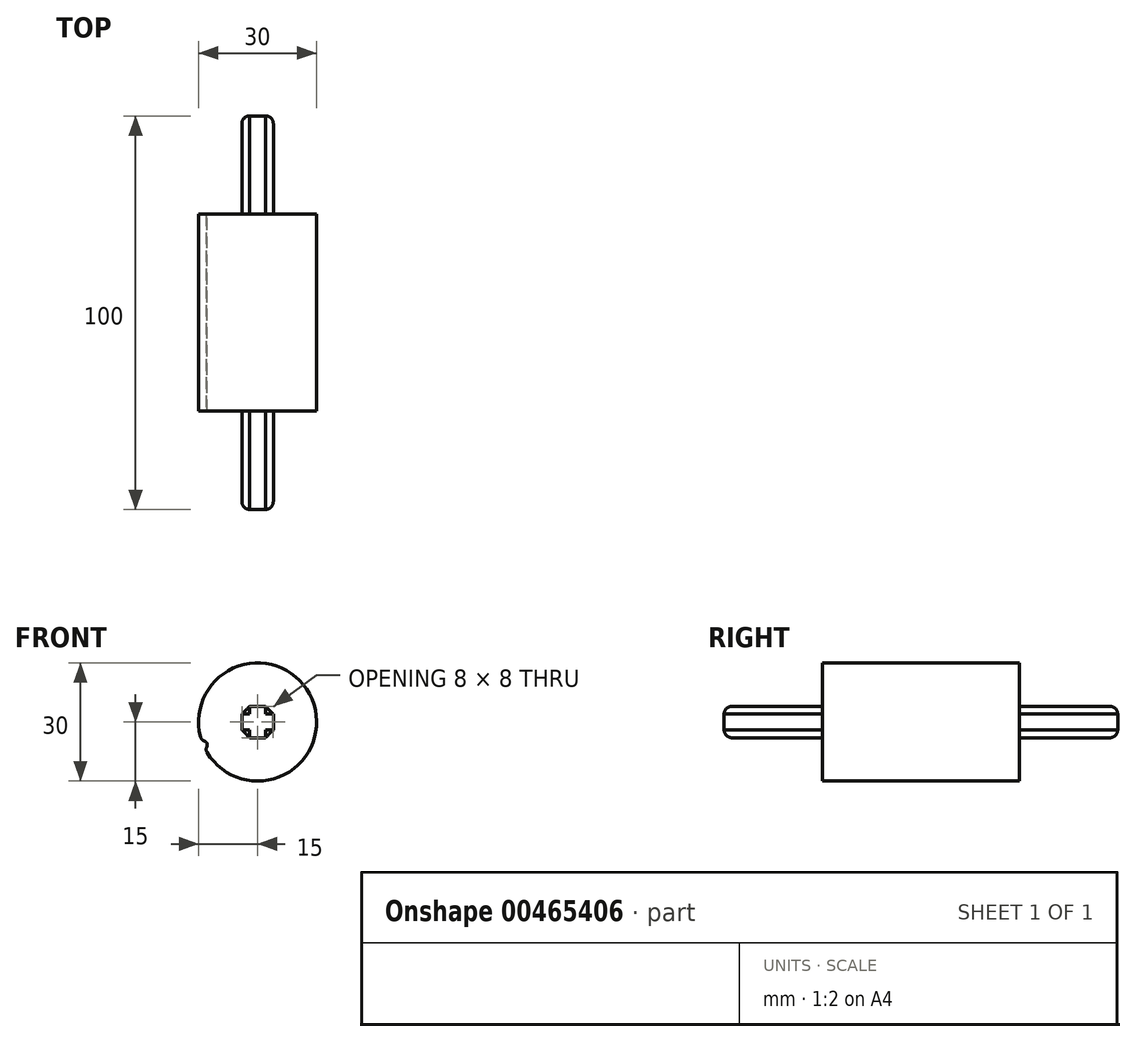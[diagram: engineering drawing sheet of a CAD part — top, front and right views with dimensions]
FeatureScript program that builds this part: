
annotation { "Feature Type Name" : "Feature", "Feature Type Description" : "" }
export const myFeature = defineFeature(function(context is Context, id is Id, definition is map)
    precondition{}
    {
        {
            var Q0;
            Q0=qCreatedBy(makeId("Front.planeOp"),FACE);
            var sketch = newSketch(context, id + "F0", { "sketchPlane" : qUnion([Q0])});
            skCircle(sketch, "E0", {"center": v(0, 0) * mm, "radius": 15 * mm});
            skSolve(sketch);
        }
        {
            var Q0;
            Q0 = qSketchRegion(id + "F0", true);
            extrude(context, id + "F1", {"entities" : qUnion([Q0]), "depth" : 25 * mm});
        }
        {
            var Q0;
            Q0=makeQuery(id+"F1.opExtrude","CAP_FACE",FACE,{"disambiguationData":[OSD([sQuery(id+"F0.wireOp",EDGE,"E0")])],"isStart":false});
            var sketch = newSketch(context, id + "F2", { "sketchPlane" : qUnion([Q0])});
            skLineSegment(sketch, "E1.bottom", {"start": v(4, -4) * mm, "end": v(-4, -4) * mm});
            skLineSegment(sketch, "E1.top", {"start": v(4, 4) * mm, "end": v(-4, 4) * mm});
            skLineSegment(sketch, "E1.left", {"start": v(4, -4) * mm, "end": v(4, 4) * mm});
            skLineSegment(sketch, "E1.right", {"start": v(-4, -4) * mm, "end": v(-4, 4) * mm});
            skCircle(sketch, "E2", {"center": v(13.4, -6.73) * mm, "radius": 1 * mm});
            skSolve(sketch);
        }
        {
            var Q0;
            Q0=makeQuery(id+"F2.imprint","IMPRINT",FACE,{"disambiguationData":[TD([[makeQuery(id+"F2.imprint","IMPRINT",EDGE,{"derivedFrom":sQuery(id+"F2.wireOp",EDGE,"E1.bottom")}),-1.0]])]});
            extrude(context, id + "F3", {"entities" : qUnion([Q0]), "operationType" : NewBodyOperationType.ADD, "depth" : 25 * mm});
        }
        {
            var Q0;
            Q0=makeQuery(id+"F1.opExtrude","CAP_FACE",FACE,{"disambiguationData":[OSD([sQuery(id+"F0.wireOp",EDGE,"E0")])],"isStart":true});
            var sketch = newSketch(context, id + "F4", { "sketchPlane" : qUnion([Q0])});
            skCircle(sketch, "E3", {"center": v(13.82, -5.83) * mm, "radius": 1.04 * mm});
            skSolve(sketch);
        }
        {
            var Q0;
            {var subQ0=sQuery(id+"F4.wireOp",EDGE,"E3");var subQ1=makeQuery(id+"F1.opExtrude","CAP_EDGE",EDGE,{"disambiguationData":[OSD([sQuery(id+"F0.wireOp",EDGE,"E0")])],"isStart":true});var subQ2=makeQuery(id+"F4.imprint","INTERSECT",VERTEX,{"disambiguationData":[OD(0.0)],"derivedFrom":[subQ1,subQ0]});Q0=makeQuery(id+"F4.imprint","IMPRINT",FACE,{"disambiguationData":[TD([[makeQuery(id+"F4.imprint","IMPRINT",EDGE,{"disambiguationData":[TD([[subQ2,1.0]])],"derivedFrom":subQ0}),1.0]])]});}
            var Q1;
            {var subQ0=sQuery(id+"F4.wireOp",EDGE,"E3");var subQ1=makeQuery(id+"F1.opExtrude","CAP_EDGE",EDGE,{"disambiguationData":[OSD([sQuery(id+"F0.wireOp",EDGE,"E0")])],"isStart":true});var subQ2=makeQuery(id+"F4.imprint","INTERSECT",VERTEX,{"disambiguationData":[OD(0.0)],"derivedFrom":[subQ1,subQ0]});Q1=makeQuery(id+"F4.imprint","IMPRINT",FACE,{"disambiguationData":[TD([[makeQuery(id+"F4.imprint","IMPRINT",EDGE,{"disambiguationData":[TD([[subQ2,-1.0]])],"derivedFrom":subQ0}),1.0]])]});}
            var Q2;
            Q2=sQuery(id+"F4.wireOp",EDGE,"E3");
            extrude(context, id + "F5", {"entities" : qUnion([Q0, Q1]), "operationType" : NewBodyOperationType.REMOVE, "surfaceEntities" : qUnion([Q2]), "oppositeDirection" : true, "depth" : 25 * mm});
        }
        {
            var Q0;
            Q0=qCreatedBy(makeId("Right.planeOp"),FACE);
            var sketch = newSketch(context, id + "F6", { "sketchPlane" : qUnion([Q0])});
            skLineSegment(sketch, "E4", {"start": v(0, 0) * mm, "end": v(-24.96, 0) * mm});
            skSolve(sketch);
        }
        {
            var Q0;
            Q0=makeQuery(id+"F3.opExtrude","CAP_EDGE",EDGE,{"disambiguationData":[OSD([sQuery(id+"F2.wireOp",EDGE,"E1.left")])],"isStart":false});
            var Q1;
            Q1=makeQuery(id+"F3.opExtrude","CAP_EDGE",EDGE,{"disambiguationData":[OSD([sQuery(id+"F2.wireOp",EDGE,"E1.bottom")])],"isStart":false});
            var Q2;
            Q2=makeQuery(id+"F3.opExtrude","CAP_EDGE",EDGE,{"disambiguationData":[OSD([sQuery(id+"F2.wireOp",EDGE,"E1.right")])],"isStart":false});
            var Q3;
            Q3=makeQuery(id+"F3.opExtrude","CAP_EDGE",EDGE,{"disambiguationData":[OSD([sQuery(id+"F2.wireOp",EDGE,"E1.top")])],"isStart":false});
            fillet(context, id + "F7", {"entities" : qUnion([Q0, Q1, Q2, Q3]), "radius" : 2 * mm, "tangentPropagation" : true, "allowEdgeOverflow" : false});
        }
        {
            var Q0;
            Q0=makeQuery(id+"F3.opExtrude","SWEPT_EDGE",EDGE,{"disambiguationData":[OSD([sQuery(id+"F2.wireOp",EDGE,"E1.bottom"),sQuery(id+"F2.wireOp",EDGE,"E1.left")])]});
            var Q1;
            Q1=makeQuery(id+"F3.opExtrude","SWEPT_EDGE",EDGE,{"disambiguationData":[OSD([sQuery(id+"F2.wireOp",EDGE,"E1.top"),sQuery(id+"F2.wireOp",EDGE,"E1.left")])]});
            var Q2;
            Q2=makeQuery(id+"F3.opExtrude","SWEPT_EDGE",EDGE,{"disambiguationData":[OSD([sQuery(id+"F2.wireOp",EDGE,"E1.top"),sQuery(id+"F2.wireOp",EDGE,"E1.right")])]});
            var Q3;
            Q3=makeQuery(id+"F3.opExtrude","SWEPT_EDGE",EDGE,{"disambiguationData":[OSD([sQuery(id+"F2.wireOp",EDGE,"E1.bottom"),sQuery(id+"F2.wireOp",EDGE,"E1.right")])]});
            chamfer(context, id + "F8", {"entities" : qUnion([Q0, Q1, Q2, Q3]), "width" : 2 * mm, "tangentPropagation" : true});
        }
        {
            var Q0;
            {var subQ0=makeQuery(id+"F5.boolean.opBoolean","INTERSECT",EDGE,{"disambiguationData":[OD(1.0)],"derivedFrom":[makeQuery(id+"F1.opExtrude","SWEPT_FACE",FACE,{"disambiguationData":[OSD([sQuery(id+"F0.wireOp",EDGE,"E0")])]}),makeQuery(id+"F5.opExtrude","SWEPT_FACE",FACE,{"disambiguationData":[OSD([sQuery(id+"F4.wireOp",EDGE,"E3")])]})]});Q0=makeQuery(id+"FoqWFQG0o3ZkEiP_1.boolean.opBoolean","MERGE",EDGE,{"derivedFrom":[subQ0,makeQuery(id+"FoqWFQG0o3ZkEiP_1.opPattern","COPY",EDGE,{"derivedFrom":subQ0,"instanceName":"1"})]});}
            var Q1;
            {var subQ0=makeQuery(id+"F5.boolean.opBoolean","INTERSECT",EDGE,{"disambiguationData":[OD(0.0)],"derivedFrom":[makeQuery(id+"F1.opExtrude","SWEPT_FACE",FACE,{"disambiguationData":[OSD([sQuery(id+"F0.wireOp",EDGE,"E0")])]}),makeQuery(id+"F5.opExtrude","SWEPT_FACE",FACE,{"disambiguationData":[OSD([sQuery(id+"F4.wireOp",EDGE,"E3")])]})]});Q1=makeQuery(id+"FoqWFQG0o3ZkEiP_1.boolean.opBoolean","MERGE",EDGE,{"derivedFrom":[subQ0,makeQuery(id+"FoqWFQG0o3ZkEiP_1.opPattern","COPY",EDGE,{"derivedFrom":subQ0,"instanceName":"1"})]});}
            fillet(context, id + "F9", {"entities" : qUnion([Q0, Q1]), "radius" : 1.5 * mm, "tangentPropagation" : true, "allowEdgeOverflow" : false});
        }
        {
            var Q0;
            Q0=makeQuery(id+"F1.opExtrude","SWEPT_BODY",BODY,{"disambiguationData":[OSD([sQuery(id+"F0.wireOp",EDGE,"E0")])]});
            var Q1;
            Q1=makeQuery(id+"F1.opExtrude","CAP_FACE",FACE,{"disambiguationData":[OSD([sQuery(id+"F0.wireOp",EDGE,"E0")])],"isStart":true});
            mirror(context, id + "F10", {"operationType" : NewBodyOperationType.ADD, "entities" : qUnion([Q0]), "mirrorPlane" : qUnion([Q1])});
        }
    });
